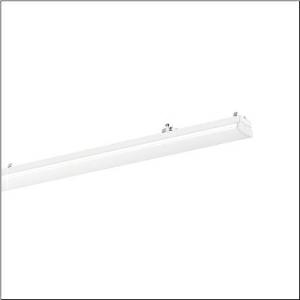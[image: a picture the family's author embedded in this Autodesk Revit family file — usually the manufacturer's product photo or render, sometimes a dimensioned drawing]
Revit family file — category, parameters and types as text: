
# Revit family: licross_r__21_recessed_opal_mo_52te1dcn485g_36e8
name_source: partatom
category: Lighting Fixtures
units: mm (PartAtom-declared; Revit-internal decimal feet)

## family parameters
Cut with Voids When Loaded = No
Host = Face
Light Source = No
Part Type = Normal
Room Calculation Point = No
Round Connector Dimension = Use Diameter
Shared = No

## types (1)
- --- (1 x LED, 8780 lm, 49.9 W, 4000K)
    Apparent Load = 50 VA
    CIE Flux Codes = 44 73 91 87 100
    Color Rendering = 80
    Color Temperature = 4000K
    Default Elevation = 1800 mm
    Description = Licross® 21 recessed opal MO, luminaire insert, of sheet steel, galvanised, coil coated, white, length: 1.500mm, width: 66mm, height: 67mm, LED rated luminous flux: 8.780lm, light colour: 840, control gear: ON/OFF Multilumen, CLOi, with plug, 3-pole, with phase selection, mains connection: 220..240V, AC, 50/60Hz, start of lifetime: 50W, end of service life: 61W, internal wiring halogen-free, primary optical cover: cover, of PMMA, light emission: direct with ceiling illumination distribution, primary light characteristic: symmetric, protection rating (complete): IP54, insulation class (complete): insulation class I (protective earthing), certification: CE, ENEC, VDE, UKCA, protection symbol: D if used in an environment with non-conductive dust loads with corresponding accessories, impact resistance: IK06, permissible ambient temperature for indoor applications: -35..+40°C, corresponds to IFS (International Featured Standards) requirements for safety and quality in the food industry, reducing of maximum allowable ambient temperature of 5°C with ceiling mounting, LABS conformity tested according to VDMA 24364:2018-05, packaging unit: 1 piece
    Height = 83 mm
    Lamp = 1 x LED
    Lamp Light Flux = 8780 lm
    Lamp Power = 49.9 W
    Lamp count = 1
    Length = 1500 mm
    Luminous efficacy = 176 lm/W
    Manufacturer = Siteco
    ModVariant = No
    Model = 52TE1DCN485G
    Mounting Place = Ceiling
    Mounting Type = Pendant
    Number of Poles = 1
    OnlyDefault = Yes
    Power Factor = 1
    Product Name = Licross® 21 recessed opal MO
    Product group = luminaire insert | ceiling pendant
    ProductGroupID = 902
    Protection Class = Protection class I
    Protection Degree = IP 54
    RLX_Detail_Level = 1
    RLX_Emergency_Light_Flux = 0 lm
    RLX_Emergency_Type = 0
    RLX_Emergency_Type_DB = No
    RlxData = <blob elided: 24789 chars, md5=6c7797f9>
    Socket = socket
    Standby Power = 0 W
    System Light Flux = 8780 lm
    System Power = 50 W
    Type Comments = factory setting: luminous flux: 100 % | (A | C | E) | 116 mA
    Type Image = l_1313666.jpg
    URL = http://relux.com
    VarID = @adj_089709
    Voltage = 0 V
    Weight = 0.00 kg
    Width = 76 mm

## geometry (parser evidence)
native form markers: Blend x4, Sweep x12
no freeform markers — native parametric forms only
